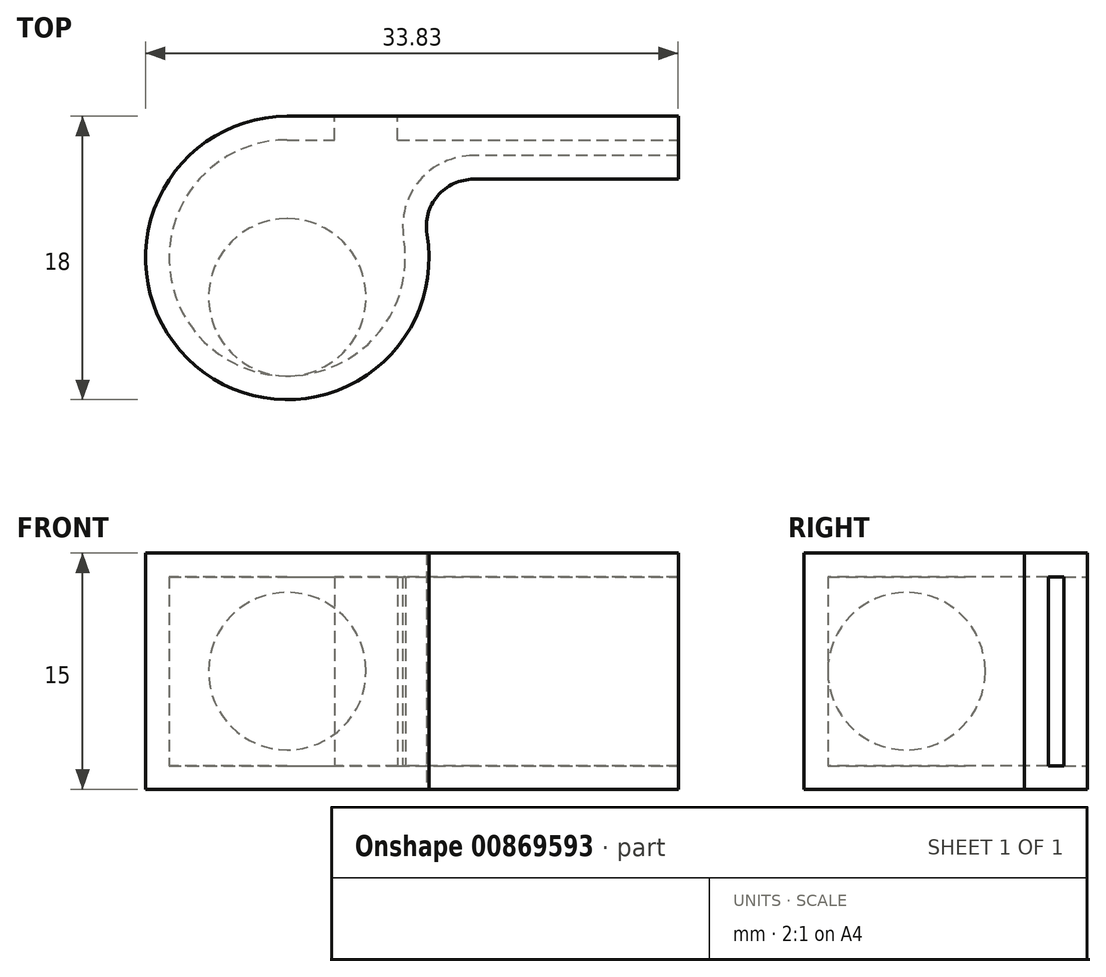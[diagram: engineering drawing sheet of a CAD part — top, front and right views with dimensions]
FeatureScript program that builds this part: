
annotation { "Feature Type Name" : "Feature", "Feature Type Description" : "" }
export const myFeature = defineFeature(function(context is Context, id is Id, definition is map)
    precondition{}
    {
        {
            var Q0;
            Q0=qCreatedBy(makeId("Top.planeOp"),FACE);
            var sketch = newSketch(context, id + "F0", { "sketchPlane" : qUnion([Q0])});
            skArc(sketch, "E0", {"start": v(0, 9) * mm, "mid": v(-5.8, -6.87) * mm, "end": v(8.87, 1.5) * mm});
            skLineSegment(sketch, "E1", {"start": v(0, 9) * mm, "end": v(24.83, 9) * mm});
            skLineSegment(sketch, "E2", {"start": v(24.83, 9) * mm, "end": v(24.83, 5) * mm});
            skLineSegment(sketch, "E3", {"start": v(24.83, 5) * mm, "end": v(11.83, 5) * mm});
            skPoint(sketch, "E4.visualSharp", {"position": v(9, 0) * mm});
            skArc(sketch, "E4.filletArc", {"start": v(11.83, 5) * mm, "mid": v(9.54, 3.94) * mm, "end": v(8.87, 1.5) * mm});
            skSolve(sketch);
        }
        {
            var Q0;
            Q0=makeQuery(id+"F0.imprint","IMPRINT",FACE,{"disambiguationData":[TD([[makeQuery(id+"F0.imprint","IMPRINT",EDGE,{"derivedFrom":sQuery(id+"F0.wireOp",EDGE,"E0")}),1.0]])]});
            extrude(context, id + "F1", {"entities" : qUnion([Q0]), "endBound" : BoundingType.SYMMETRIC, "depth" : 15 * mm, "offsetDistance" : 25 * mm});
        }
        {
            var Q0;
            Q0=makeQuery(id+"F1.opExtrude","SWEPT_FACE",FACE,{"disambiguationData":[OSD([sQuery(id+"F0.wireOp",EDGE,"E2")])]});
            shell(context, id + "F2", {"entities" : qUnion([Q0]), "thickness" : 1.5 * mm});
        }
        {
            var Q0;
            Q0=makeQuery(id+"F1.opExtrude","SWEPT_FACE",FACE,{"disambiguationData":[OSD([sQuery(id+"F0.wireOp",EDGE,"E1")])]});
            var sketch = newSketch(context, id + "F3", { "sketchPlane" : qUnion([Q0])});
            skLineSegment(sketch, "E5.bottom", {"start": v(-7, 6) * mm, "end": v(-3, 6) * mm});
            skLineSegment(sketch, "E5.top", {"start": v(-7, -6) * mm, "end": v(-3, -6) * mm});
            skLineSegment(sketch, "E5.left", {"start": v(-7, 6) * mm, "end": v(-7, -6) * mm});
            skLineSegment(sketch, "E5.right", {"start": v(-3, 6) * mm, "end": v(-3, -6) * mm});
            skSolve(sketch);
        }
        {
            var Q0;
            Q0=makeQuery(id+"F3.imprint","IMPRINT",FACE,{"disambiguationData":[TD([[makeQuery(id+"F3.imprint","IMPRINT",EDGE,{"derivedFrom":sQuery(id+"F3.wireOp",EDGE,"E5.bottom")}),-1.0]])]});
            extrude(context, id + "F4", {"entities" : qUnion([Q0]), "operationType" : NewBodyOperationType.REMOVE, "oppositeDirection" : true, "depth" : 1.5 * mm, "offsetDistance" : 25 * mm});
        }
        {
            var Q0;
            Q0=qCreatedBy(makeId("Top.planeOp"),FACE);
            var sketch = newSketch(context, id + "F5", { "sketchPlane" : qUnion([Q0])});
            skArc(sketch, "E6", {"start": v(0, -7.5) * mm, "mid": v(-5, -2.5) * mm, "end": v(0, 2.5) * mm});
            skLineSegment(sketch, "E7", {"start": v(0, 2.5) * mm, "end": v(0, -7.5) * mm});
            skSolve(sketch);
        }
        {
            var Q0;
            Q0 = qSketchRegion(id + "F5", true);
            var Q1;
            Q1=sQuery(id+"F5.wireOp",EDGE,"E7");
            revolve(context, id + "F6", {"surfaceOperationType" : NewSurfaceOperationType.NEW, "entities" : qUnion([Q0]), "axis" : qUnion([Q1]), "revolveType" : RevolveType.FULL});
        }
    });
